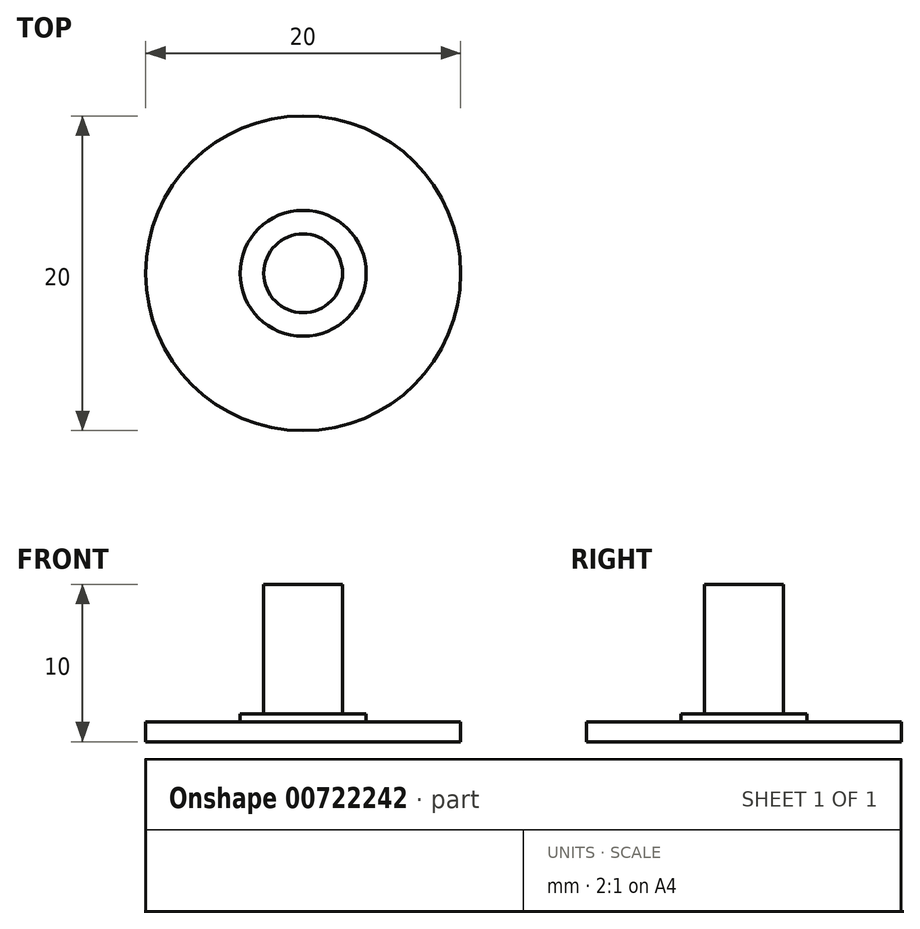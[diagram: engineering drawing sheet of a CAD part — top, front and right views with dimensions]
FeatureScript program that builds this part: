
annotation { "Feature Type Name" : "Feature", "Feature Type Description" : "" }
export const myFeature = defineFeature(function(context is Context, id is Id, definition is map)
    precondition{}
    {
        {
            var Q0;
            Q0=qCreatedBy(makeId("Top.planeOp"),FACE);
            var sketch = newSketch(context, id + "F0", { "sketchPlane" : qUnion([Q0])});
            skCircle(sketch, "E0", {"center": v(0, 0) * mm, "radius": 10 * mm});
            skCircle(sketch, "E1", {"center": v(0, 0) * mm, "radius": 2.5 * mm});
            skCircle(sketch, "E2", {"center": v(0, 0) * mm, "radius": 4 * mm});
            skSolve(sketch);
        }
        {
            var Q0;
            Q0 = qSketchRegion(id + "F0", true);
            var Q1;
            Q1=makeQuery(id+"F0.imprint","IMPRINT",FACE,{"disambiguationData":[TD([[makeQuery(id+"F0.imprint","IMPRINT",EDGE,{"derivedFrom":sQuery(id+"F0.wireOp",EDGE,"E0")}),1.0]])]});
            extrude(context, id + "F1", {"entities" : qUnion([Q0, Q1]), "depth" : 1.27 * mm, "offsetDistance" : 25.4 * mm});
        }
        {
            var Q0;
            Q0=makeQuery(id+"F0.imprint","IMPRINT",FACE,{"disambiguationData":[TD([[makeQuery(id+"F0.imprint","IMPRINT",EDGE,{"derivedFrom":sQuery(id+"F0.wireOp",EDGE,"E1")}),-1.0]])]});
            extrude(context, id + "F2", {"entities" : qUnion([Q0]), "operationType" : NewBodyOperationType.ADD, "depth" : 1.78 * mm, "offsetDistance" : 25.4 * mm});
        }
        {
            var Q0;
            Q0=makeQuery(id+"F0.imprint","IMPRINT",FACE,{"disambiguationData":[TD([[makeQuery(id+"F0.imprint","IMPRINT",EDGE,{"derivedFrom":sQuery(id+"F0.wireOp",EDGE,"E1")}),1.0]])]});
            extrude(context, id + "F3", {"entities" : qUnion([Q0]), "operationType" : NewBodyOperationType.ADD, "depth" : 10 * mm, "offsetDistance" : 25.4 * mm});
        }
    });
